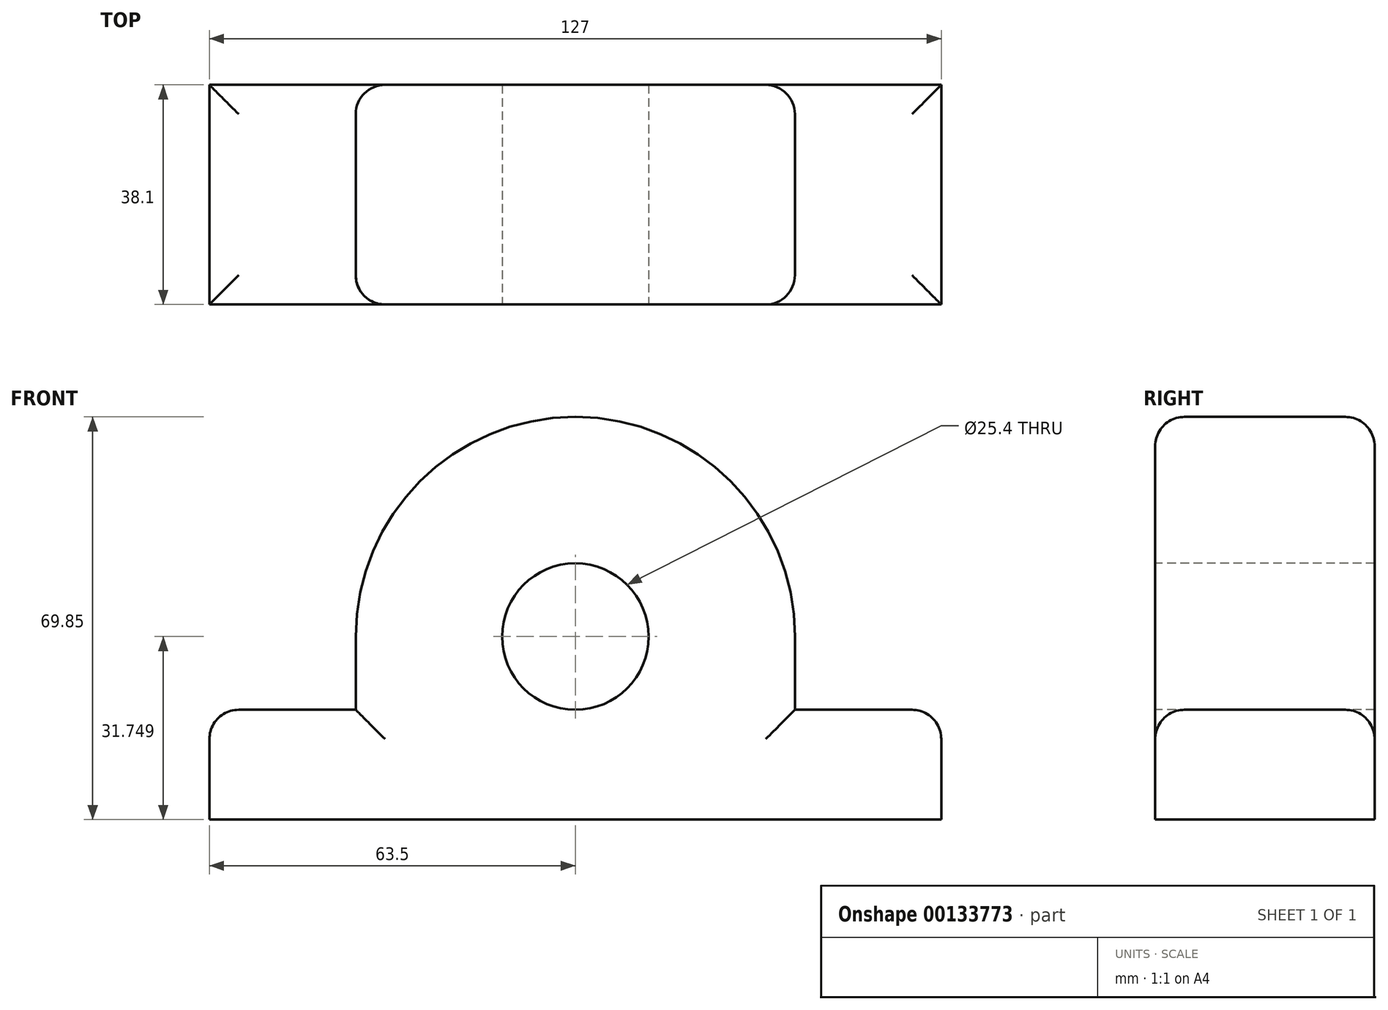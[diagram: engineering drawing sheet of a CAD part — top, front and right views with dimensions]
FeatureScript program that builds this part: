
annotation { "Feature Type Name" : "Feature", "Feature Type Description" : "" }
export const myFeature = defineFeature(function(context is Context, id is Id, definition is map)
    precondition{}
    {
        {
            var Q0;
            Q0=qCreatedBy(makeId("Front.planeOp"),FACE);
            var sketch = newSketch(context, id + "F0", { "sketchPlane" : qUnion([Q0])});
            skLineSegment(sketch, "E0", {"start": v(-25.4, 74.78) * mm, "end": v(101.6, 74.78) * mm});
            skLineSegment(sketch, "E1", {"start": v(101.6, 74.78) * mm, "end": v(101.6, 93.83) * mm});
            skLineSegment(sketch, "E2", {"start": v(101.6, 93.83) * mm, "end": v(76.2, 93.83) * mm});
            skLineSegment(sketch, "E3", {"start": v(76.2, 93.83) * mm, "end": v(76.2, 106.53) * mm});
            skLineSegment(sketch, "E4", {"start": v(-25.4, 74.78) * mm, "end": v(-25.4, 93.83) * mm});
            skLineSegment(sketch, "E5", {"start": v(-25.4, 93.83) * mm, "end": v(0, 93.83) * mm});
            skLineSegment(sketch, "E6", {"start": v(0, 93.83) * mm, "end": v(0, 106.53) * mm});
            skArc(sketch, "E7", {"start": v(76.2, 106.53) * mm, "mid": v(38.1, 144.63) * mm, "end": v(0, 106.53) * mm});
            skSolve(sketch);
        }
        {
            var Q0;
            Q0=makeQuery(id+"F0.imprint","IMPRINT",FACE,{"disambiguationData":[TD([[makeQuery(id+"F0.imprint","IMPRINT",EDGE,{"derivedFrom":sQuery(id+"F0.wireOp",EDGE,"E0")}),1.0]])]});
            extrude(context, id + "F1", {"entities" : qUnion([Q0]), "depth" : 38.1 * mm});
        }
        {
            var Q0;
            Q0=makeQuery(id+"F1.opExtrude","CAP_EDGE",EDGE,{"disambiguationData":[OSD([sQuery(id+"F0.wireOp",EDGE,"E7")])],"isStart":false});
            var Q1;
            Q1=makeQuery(id+"F1.opExtrude","CAP_EDGE",EDGE,{"disambiguationData":[OSD([sQuery(id+"F0.wireOp",EDGE,"E7")])],"isStart":true});
            var Q2;
            Q2=makeQuery(id+"F1.opExtrude","CAP_EDGE",EDGE,{"disambiguationData":[OSD([sQuery(id+"F0.wireOp",EDGE,"E2")])],"isStart":false});
            var Q3;
            Q3=makeQuery(id+"F1.opExtrude","SWEPT_EDGE",EDGE,{"disambiguationData":[OSD([sQuery(id+"F0.wireOp",EDGE,"E1"),sQuery(id+"F0.wireOp",EDGE,"E2")])]});
            var Q4;
            Q4=makeQuery(id+"F1.opExtrude","CAP_EDGE",EDGE,{"disambiguationData":[OSD([sQuery(id+"F0.wireOp",EDGE,"E2")])],"isStart":true});
            var Q5;
            Q5=makeQuery(id+"F1.opExtrude","CAP_EDGE",EDGE,{"disambiguationData":[OSD([sQuery(id+"F0.wireOp",EDGE,"E5")])],"isStart":false});
            var Q6;
            Q6=makeQuery(id+"F1.opExtrude","CAP_EDGE",EDGE,{"disambiguationData":[OSD([sQuery(id+"F0.wireOp",EDGE,"E5")])],"isStart":true});
            var Q7;
            Q7=makeQuery(id+"F1.opExtrude","SWEPT_EDGE",EDGE,{"disambiguationData":[OSD([sQuery(id+"F0.wireOp",EDGE,"E4"),sQuery(id+"F0.wireOp",EDGE,"E5")])]});
            fillet(context, id + "F2", {"entities" : qUnion([Q0, Q1, Q2, Q3, Q4, Q5, Q6, Q7]), "radius" : 5.08 * mm, "tangentPropagation" : true, "allowEdgeOverflow" : false});
        }
        {
            var Q0;
            Q0=makeQuery(id+"F1.opExtrude","CAP_FACE",FACE,{"disambiguationData":[OSD([sQuery(id+"F0.wireOp",EDGE,"E0"),sQuery(id+"F0.wireOp",EDGE,"E1"),sQuery(id+"F0.wireOp",EDGE,"E2"),sQuery(id+"F0.wireOp",EDGE,"E3"),sQuery(id+"F0.wireOp",EDGE,"E4"),sQuery(id+"F0.wireOp",EDGE,"E5"),sQuery(id+"F0.wireOp",EDGE,"E6"),sQuery(id+"F0.wireOp",EDGE,"E7")])],"isStart":false});
            var sketch = newSketch(context, id + "F3", { "sketchPlane" : qUnion([Q0])});
            skCircle(sketch, "E8", {"center": v(38.1, 106.53) * mm, "radius": 12.7 * mm});
            skSolve(sketch);
        }
        {
            var Q0;
            Q0=makeQuery(id+"F3.imprint","IMPRINT",FACE,{"disambiguationData":[TD([[makeQuery(id+"F3.imprint","IMPRINT",EDGE,{"derivedFrom":sQuery(id+"F3.wireOp",EDGE,"E8")}),1.0]])]});
            extrude(context, id + "F4", {"entities" : qUnion([Q0]), "operationType" : NewBodyOperationType.REMOVE, "oppositeDirection" : true, "depth" : 38.1 * mm});
        }
    });
